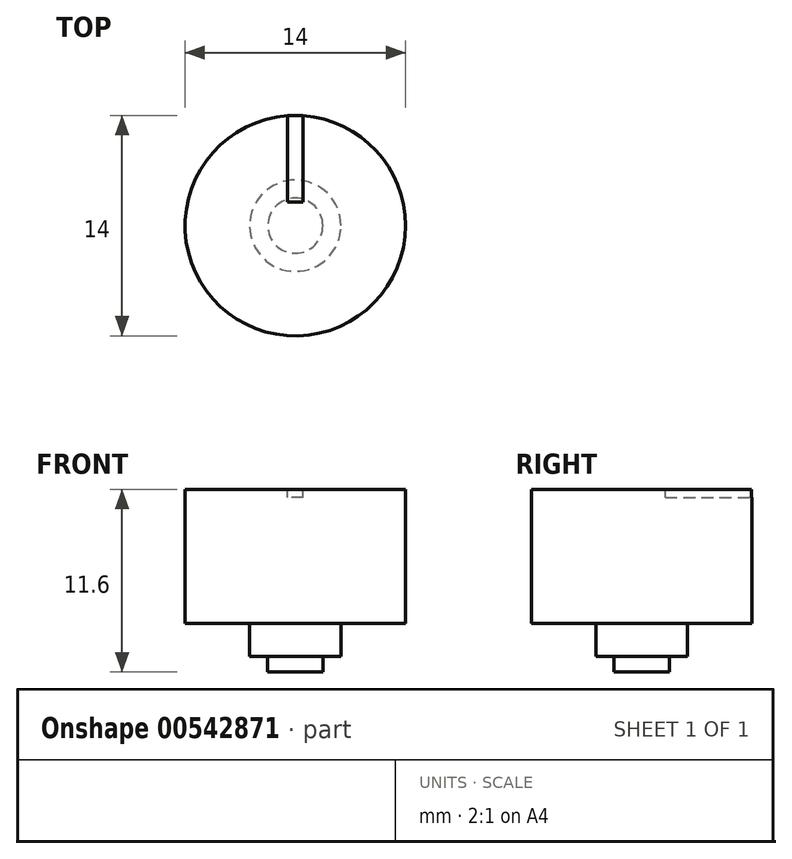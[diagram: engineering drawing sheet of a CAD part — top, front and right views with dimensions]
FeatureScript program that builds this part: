
annotation { "Feature Type Name" : "Feature", "Feature Type Description" : "" }
export const myFeature = defineFeature(function(context is Context, id is Id, definition is map)
    precondition{}
    {
        {
            var Q0;
            Q0=qCreatedBy(makeId("Front.planeOp"),FACE);
            var sketch = newSketch(context, id + "F0", { "sketchPlane" : qUnion([Q0])});
            skLineSegment(sketch, "E0", {"start": v(0, -1) * mm, "end": v(-1.75, -1) * mm});
            skLineSegment(sketch, "E1", {"start": v(-1.75, -1) * mm, "end": v(-1.75, 0) * mm});
            skLineSegment(sketch, "E2", {"start": v(-1.75, 0) * mm, "end": v(-2.9, 0) * mm});
            skLineSegment(sketch, "E3", {"start": v(-2.9, 0) * mm, "end": v(-2.9, 2.1) * mm});
            skLineSegment(sketch, "E4", {"start": v(-2.9, 2.1) * mm, "end": v(-7, 2.1) * mm});
            skLineSegment(sketch, "E5", {"start": v(-7, 2.1) * mm, "end": v(-7, 10.6) * mm});
            skLineSegment(sketch, "E6", {"start": v(-7, 10.6) * mm, "end": v(0, 10.6) * mm});
            skLineSegment(sketch, "E7", {"start": v(0, 10.6) * mm, "end": v(0, -1) * mm});
            skSolve(sketch);
        }
        {
            var Q0;
            Q0 = qSketchRegion(id + "F0", true);
            var Q1;
            Q1=sQuery(id+"F0.wireOp",EDGE,"E7");
            revolve(context, id + "F1", {"entities" : qUnion([Q0]), "axis" : qUnion([Q1]), "revolveType" : RevolveType.FULL});
        }
        {
            var Q0;
            Q0=makeQuery(id+"F1.opRevolve","SWEPT_FACE",FACE,{"disambiguationData":[OSD([sQuery(id+"F0.wireOp",EDGE,"E6")])]});
            var sketch = newSketch(context, id + "F2", { "sketchPlane" : qUnion([Q0])});
            skLineSegment(sketch, "E8", {"start": v(0.5, 1.5) * mm, "end": v(-0.5, 1.5) * mm});
            skLineSegment(sketch, "E9", {"start": v(-0.5, 1.5) * mm, "end": v(-0.5, 6.98) * mm});
            skLineSegment(sketch, "E10", {"start": v(0.5, 1.5) * mm, "end": v(0.5, 6.98) * mm});
            skSolve(sketch);
        }
        {
            var Q0;
            Q0 = qSketchRegion(id + "F2", true);
            var Q1;
            Q1=makeQuery(id+"F2.imprint","IMPRINT",FACE,{"disambiguationData":[TD([[makeQuery(id+"F2.imprint","IMPRINT",EDGE,{"derivedFrom":sQuery(id+"F2.wireOp",EDGE,"E8")}),-1.0]])]});
            extrude(context, id + "F3", {"entities" : qUnion([Q0, Q1]), "operationType" : NewBodyOperationType.REMOVE, "oppositeDirection" : true, "depth" : 0.5 * mm, "offsetDistance" : 25 * mm});
        }
    });
